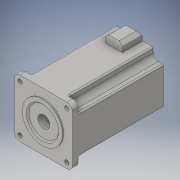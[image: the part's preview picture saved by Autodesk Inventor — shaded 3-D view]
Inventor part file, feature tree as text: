
AUTODESK INVENTOR PART (.ipt)
format: ipt  version: 2016 (Build 200138000, 138)  size: 365,568 bytes
history: native  units: mm
features: extrude x13, sketch x13, chamfer x5, projected_geometry x4, fillet x3, hole x1, plane x1
ambient origin geometry x8: Origin, YZ Plane, XZ Plane, XY Plane, X Axis, Y Axis, Z Axis, Center Point
bodies: Solid1 (feature_tree)
feature tree (40):
  extrude  "Extrusion1"  Depth=86.0mm
  extrude  "Extrusion2"  Depth=140.0mm
  extrude  "Extrusion3"  Depth=1.5mm
  hole  "Hole1"  [1 undecoded]
  plane  "Work Plane1"
  extrude  "Extrusion4"  Depth=13.0mm TaperAngle=0.0deg
  sketch  "Sketch6"  dims[d13=3.0mm d14=6.0mm d15=4.0mm d16=2.0mm d17=90.0deg d18=13.0mm d19=0.0mm d24=2.438mm d25=0.0mm]
  extrude  "Extrusion6"  Depth=69.6mm
  extrude  "Extrusion7"  Depth=120.0mm TaperAngle=0.0deg
  chamfer  "Chamfer1"  Distance=13.0mm
  fillet  "Fillet1"  Radius=8.0mm
  chamfer  "Chamfer2"  Distance=5.0mm Angle=45.0deg
  chamfer  "Chamfer3"  Distance=1.0mm Angle=45.0deg
  extrude  "Extrusion8"  Depth=56.0mm
  extrude  "Extrusion9"  Depth=3.0mm TaperAngle=45.0deg
  chamfer  "Chamfer4"  Distance=2.0mm
  fillet  "Fillet3"  Radius=15.0mm
  extrude  "Extrusion10"  Depth=15.0mm
  fillet  "Fillet4"  Radius=40.0mm
  extrude  "Extrusion11"  Depth=130.0mm TaperAngle=0.0deg
  chamfer  "Chamfer5"  Distance=2.0mm
  extrude  "Extrusion13"  Depth=8.0mm
  extrude  "Extrusion14"  Depth=2.0mm TaperAngle=0.0deg
  extrude  "Extrusion15"  Depth=2.0mm TaperAngle=45.0deg
  sketch  "Sketch1"  dims[d0=86.0mm d1=86.0mm]
  sketch  "Sketch2"  dims[d2=140.0mm d3=0.0mm d5=60.0mm]
  sketch  "Sketch3"  dims[d6=1.5mm d7=0.0mm d8=14.0mm]
  sketch  "Sketch5"  dims[d9=40.0mm d10=0.0mm d11=10.0mm d12=10.0mm]
  projected_geometry  "Projected Loop1"
  sketch  "Sketch7"  dims[d36=6.5mm d37=69.6mm]
  projected_geometry  "Projected Loop2"
  sketch  "Sketch8"  dims[d38=69.6mm d39=120.0mm d40=0.0mm]
  sketch  "Sketch9"  dims[d41=25.0mm]
  projected_geometry  "Projected Loop3"
  sketch  "Sketch10"  dims[d42=30.0mm]
  sketch  "Sketch11"  dims[d43=5.0mm d46=13.0mm d47=0.0mm]
  sketch  "Sketch13"  dims[d48=5.0mm d49=7.0mm d50=45.0deg d51=8.0mm d53=5.0mm d54=7.0mm d55=45.0deg d56=1.0mm d57=7.0mm d58=45.0deg]
  projected_geometry  "Projected Loop5"
  sketch  "Sketch14"  dims[d59=3.0mm d60=0.0mm d61=56.0mm]
  sketch  "Sketch15"  dims[d62=3.0mm d63=0.0mm d64=3.0mm d65=7.0mm d66=45.0deg d67=2.0mm d71=15.0mm d72=15.0mm d73=40.0mm d75=360.0deg d77=130.0mm d78=0.0mm d79=2.0mm d81=8.0mm d82=2.0mm d83=0.0mm d84=2.0mm d85=7.0mm d86=45.0deg d90=13.0mm d91=10.0mm d92=0.0mm d93=10.0mm d94=0.0mm d95=10.0mm d96=0.0mm]
note: 1 required parameter value undecoded (feature->parameter linkage not recoverable at this tier; creation-order binding heuristic only, values carry confidence <= 0.55)
